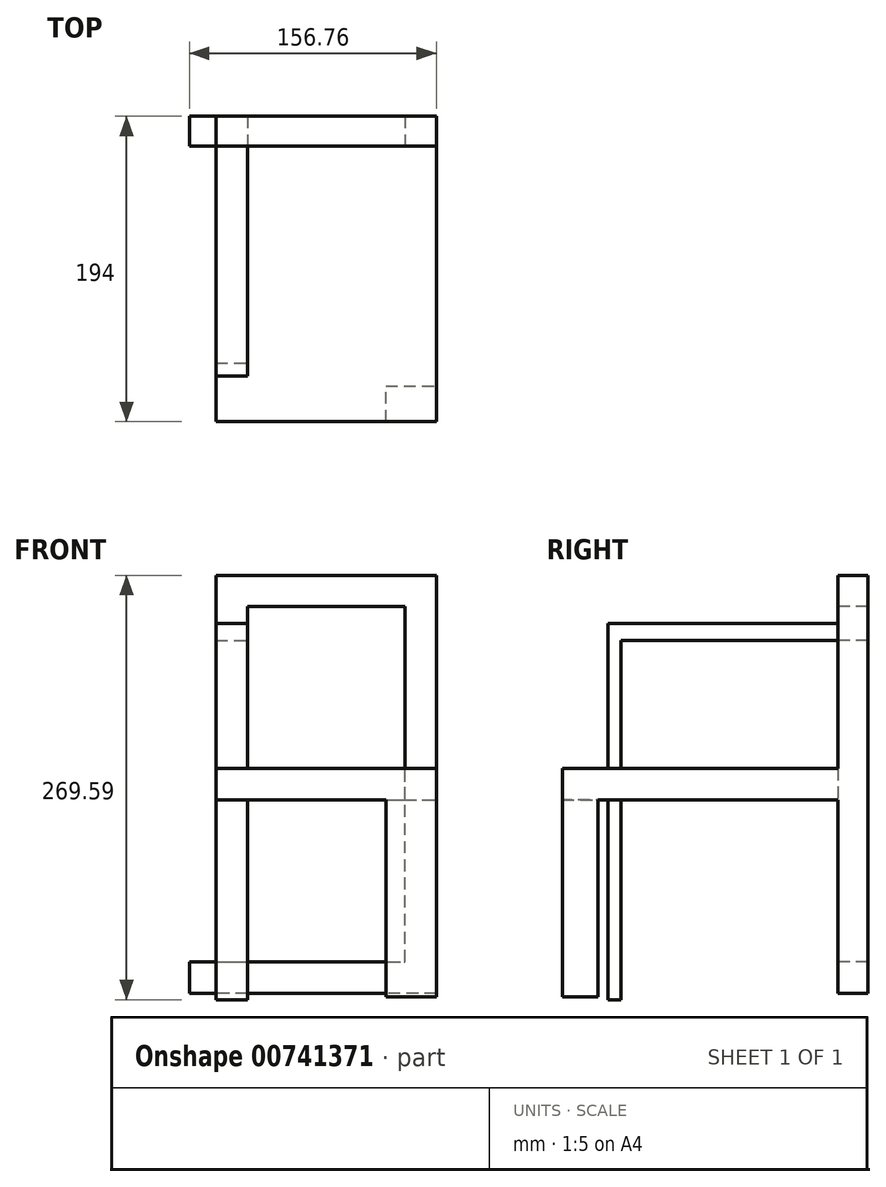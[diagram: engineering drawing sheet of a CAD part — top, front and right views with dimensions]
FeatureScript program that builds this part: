
annotation { "Feature Type Name" : "Feature", "Feature Type Description" : "" }
export const myFeature = defineFeature(function(context is Context, id is Id, definition is map)
    precondition{}
    {
        {
            var Q0;
            Q0=qCreatedBy(makeId("Top.planeOp"),FACE);
            var sketch = newSketch(context, id + "F0", { "sketchPlane" : qUnion([Q0])});
            skLineSegment(sketch, "E0.bottom", {"start": v(-26.9, 103.93) * mm, "end": v(113.1, 103.93) * mm});
            skLineSegment(sketch, "E0.top", {"start": v(-26.9, -46.07) * mm, "end": v(113.1, -46.07) * mm});
            skLineSegment(sketch, "E0.left", {"start": v(-26.9, 103.93) * mm, "end": v(-26.9, -46.07) * mm});
            skLineSegment(sketch, "E0.right", {"start": v(113.1, 103.93) * mm, "end": v(113.1, -46.07) * mm});
            skSolve(sketch);
        }
        {
            var Q0;
            Q0=makeQuery(id+"F0.imprint","IMPRINT",FACE,{"disambiguationData":[TD([[makeQuery(id+"F0.imprint","IMPRINT",EDGE,{"derivedFrom":sQuery(id+"F0.wireOp",EDGE,"E0.bottom")}),-1.0]])]});
            extrude(context, id + "F1", {"entities" : qUnion([Q0]), "depth" : 20 * mm, "offsetDistance" : 25 * mm});
        }
        {
            var Q0;
            Q0=makeQuery(id+"F1.opExtrude","SWEPT_FACE",FACE,{"disambiguationData":[OSD([sQuery(id+"F0.wireOp",EDGE,"E0.bottom")])]});
            extrude(context, id + "F2", {"entities" : qUnion([Q0]), "operationType" : NewBodyOperationType.ADD, "depth" : 25 * mm, "offsetDistance" : 25 * mm});
        }
        {
            var Q0;
            Q0=makeQuery(id+"F2.opExtrude","CAP_FACE",FACE,{"disambiguationData":[OSD([sQuery(id+"F0.wireOp",EDGE,"E0.bottom")])],"isStart":false});
            var sketch = newSketch(context, id + "F3", { "sketchPlane" : qUnion([Q0])});
            skLineSegment(sketch, "E1", {"start": v(26.9, 101.1) * mm, "end": v(26.9, 142.7) * mm});
            skLineSegment(sketch, "E2", {"start": v(26.9, 142.7) * mm, "end": v(-113.1, 142.7) * mm});
            skLineSegment(sketch, "E3", {"start": v(-113.1, 142.7) * mm, "end": v(-113.1, -122.8) * mm});
            skLineSegment(sketch, "E4", {"start": v(-113.1, -122.8) * mm, "end": v(43.65, -122.8) * mm});
            skLineSegment(sketch, "E5", {"start": v(43.65, -122.8) * mm, "end": v(43.65, -102.8) * mm});
            skLineSegment(sketch, "E6", {"start": v(43.65, -102.8) * mm, "end": v(-93.1, -102.8) * mm});
            skLineSegment(sketch, "E7", {"start": v(-93.1, -102.8) * mm, "end": v(-93.1, 122.7) * mm});
            skLineSegment(sketch, "E8", {"start": v(-93.1, 122.7) * mm, "end": v(6.9, 122.7) * mm});
            skLineSegment(sketch, "E9", {"start": v(6.9, 122.7) * mm, "end": v(6.9, 101.1) * mm});
            skLineSegment(sketch, "E10", {"start": v(6.9, 101.1) * mm, "end": v(26.9, 101.1) * mm});
            skSolve(sketch);
        }
        {
            var Q0;
            Q0 = qSketchRegion(id + "F3", true);
            extrude(context, id + "F4", {"entities" : qUnion([Q0]), "operationType" : NewBodyOperationType.ADD, "depth" : 19 * mm, "offsetDistance" : 25 * mm});
        }
        {
            var Q0;
            {var subQ0=sQuery(id+"F3.wireOp",EDGE,"E7");var subQ1=sQuery(id+"F3.wireOp",EDGE,"E2");var subQ4=sQuery(id+"F3.wireOp",EDGE,"E1");var subQ5=sQuery(id+"F3.wireOp",EDGE,"E3");var subQ6=sQuery(id+"F3.wireOp",EDGE,"E10");var subQ7=sQuery(id+"F3.wireOp",EDGE,"E8");var subQ8=sQuery(id+"F3.wireOp",EDGE,"E9");Q0=makeQuery(id+"F4.boolean.opBoolean","SPLIT",FACE,{"disambiguationData":[TD([makeQuery(id+"F4.opExtrude","SWEPT_FACE",FACE,{"disambiguationData":[OSD([subQ4])]})])],"derivedFrom":makeQuery(id+"F4.opExtrude","CAP_FACE",FACE,{"disambiguationData":[OSD([subQ4,subQ1,subQ5,sQuery(id+"F3.wireOp",EDGE,"E4"),sQuery(id+"F3.wireOp",EDGE,"E5"),sQuery(id+"F3.wireOp",EDGE,"E6"),subQ0,subQ7,subQ8,subQ6])],"isStart":true})});}
            var sketch = newSketch(context, id + "F5", { "sketchPlane" : qUnion([Q0])});
            skLineSegment(sketch, "E11.bottom", {"start": v(-26.9, 101.1) * mm, "end": v(-6.9, 101.1) * mm});
            skLineSegment(sketch, "E11.top", {"start": v(-26.9, 111.9) * mm, "end": v(-6.9, 111.9) * mm});
            skLineSegment(sketch, "E11.left", {"start": v(-26.9, 101.1) * mm, "end": v(-26.9, 111.9) * mm});
            skLineSegment(sketch, "E11.right", {"start": v(-6.9, 101.1) * mm, "end": v(-6.9, 111.9) * mm});
            skSolve(sketch);
        }
        {
            var Q0;
            Q0 = qSketchRegion(id + "F5", true);
            extrude(context, id + "F6", {"entities" : qUnion([Q0]), "operationType" : NewBodyOperationType.ADD, "depth" : 146 * mm, "offsetDistance" : 25 * mm});
        }
        {
            var Q0;
            {var subQ0=sQuery(id+"F0.wireOp",EDGE,"E0.bottom");Q0=makeQuery(id+"F2.boolean.opBoolean","MERGE",FACE,{"derivedFrom":[makeQuery(id+"F1.opExtrude","CAP_FACE",FACE,{"disambiguationData":[OSD([subQ0,sQuery(id+"F0.wireOp",EDGE,"E0.top"),sQuery(id+"F0.wireOp",EDGE,"E0.left"),sQuery(id+"F0.wireOp",EDGE,"E0.right")])],"isStart":true}),makeQuery(id+"F2.opExtrude","SWEPT_FACE",FACE,{"disambiguationData":[OSD([subQ0]),TDD([makeQuery(id+"F1.opExtrude","CAP_EDGE",EDGE,{"disambiguationData":[OSD([subQ0])],"isStart":true})])]})]});}
            var sketch = newSketch(context, id + "F7", { "sketchPlane" : qUnion([Q0])});
            skLineSegment(sketch, "E12.bottom", {"start": v(80.98, 46.07) * mm, "end": v(113.1, 46.07) * mm});
            skLineSegment(sketch, "E12.top", {"start": v(80.98, 23.54) * mm, "end": v(113.1, 23.54) * mm});
            skLineSegment(sketch, "E12.left", {"start": v(80.98, 46.07) * mm, "end": v(80.98, 23.54) * mm});
            skLineSegment(sketch, "E12.right", {"start": v(113.1, 46.07) * mm, "end": v(113.1, 23.54) * mm});
            skSolve(sketch);
        }
        {
            var Q0;
            Q0 = qSketchRegion(id + "F7", true);
            extrude(context, id + "F8", {"entities" : qUnion([Q0]), "operationType" : NewBodyOperationType.ADD, "depth" : 125 * mm, "offsetDistance" : 25 * mm});
        }
        {
            var Q0;
            Q0=makeQuery(id+"F6.boolean.opBoolean","MERGE",FACE,{"derivedFrom":[makeQuery(id+"F4.opExtrude","SWEPT_FACE",FACE,{"disambiguationData":[OSD([sQuery(id+"F3.wireOp",EDGE,"E10")])]}),makeQuery(id+"F6.opExtrude","SWEPT_FACE",FACE,{"disambiguationData":[OSD([sQuery(id+"F5.wireOp",EDGE,"E11.bottom")])]})]});
            var sketch = newSketch(context, id + "F9", { "sketchPlane" : qUnion([Q0])});
            skLineSegment(sketch, "E13.bottom", {"start": v(-26.9, 17.07) * mm, "end": v(-6.9, 17.07) * mm});
            skLineSegment(sketch, "E13.top", {"start": v(-26.9, 8.78) * mm, "end": v(-6.9, 8.78) * mm});
            skLineSegment(sketch, "E13.left", {"start": v(-26.9, 17.07) * mm, "end": v(-26.9, 8.78) * mm});
            skLineSegment(sketch, "E13.right", {"start": v(-6.9, 17.07) * mm, "end": v(-6.9, 8.78) * mm});
            skSolve(sketch);
        }
        {
            var Q0;
            Q0 = qSketchRegion(id + "F9", true);
            extrude(context, id + "F10", {"entities" : qUnion([Q0]), "operationType" : NewBodyOperationType.ADD, "depth" : 228 * mm, "offsetDistance" : 25 * mm});
        }
    });
